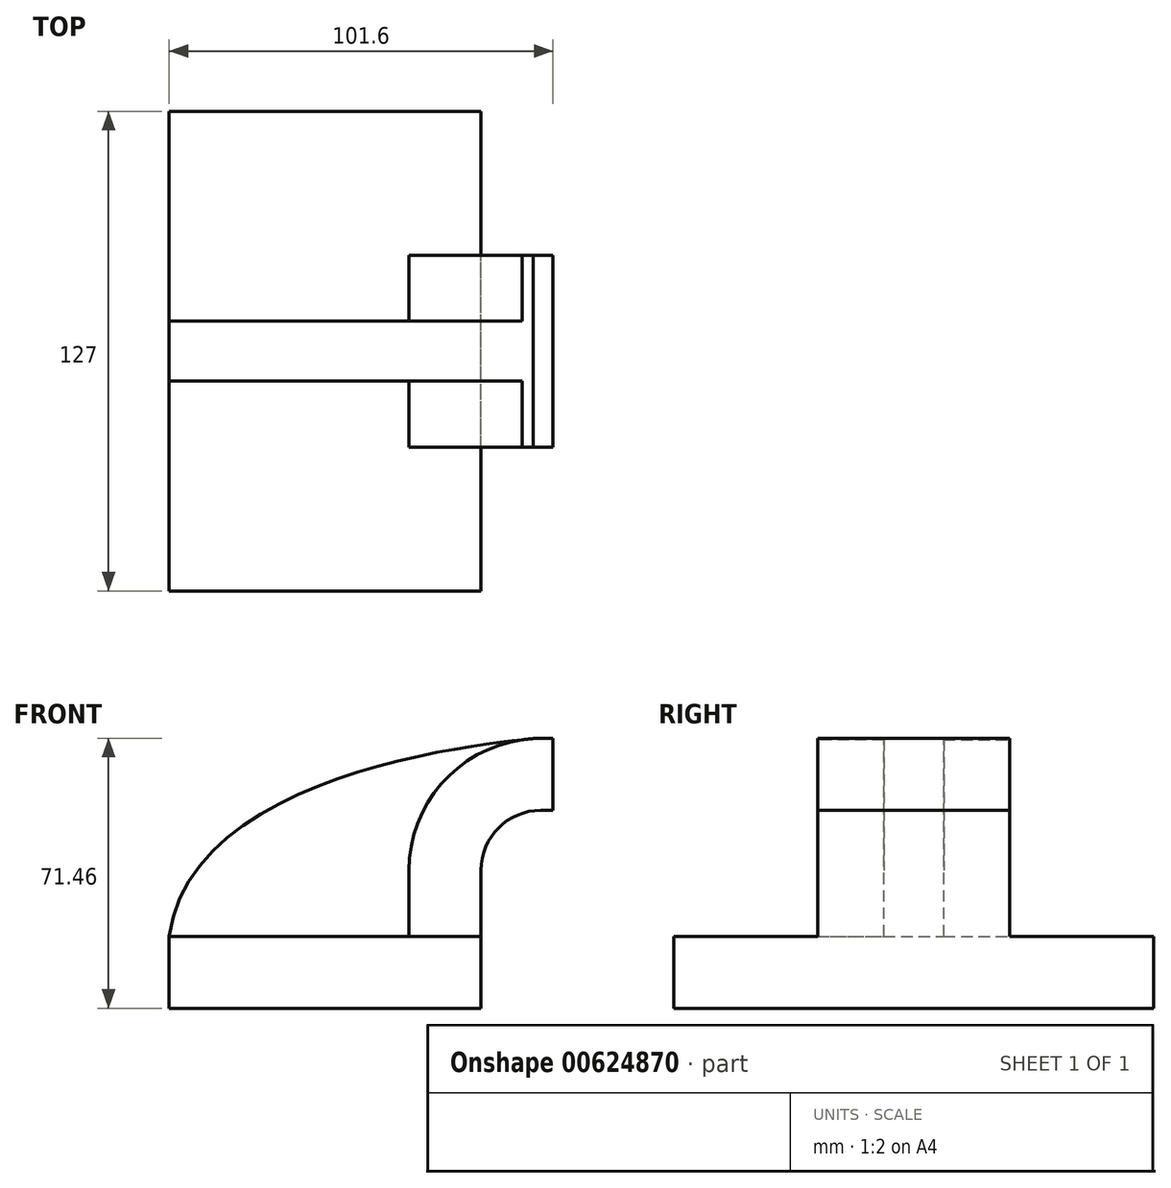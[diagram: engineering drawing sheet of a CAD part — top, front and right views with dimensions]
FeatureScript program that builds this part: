
annotation { "Feature Type Name" : "Feature", "Feature Type Description" : "" }
export const myFeature = defineFeature(function(context is Context, id is Id, definition is map)
    precondition{}
    {
        {
            var Q0;
            Q0=qCreatedBy(makeId("Front.planeOp"),FACE);
            var sketch = newSketch(context, id + "F0", { "sketchPlane" : qUnion([Q0])});
            skLineSegment(sketch, "E0.bottom", {"start": v(-41.28, -9.53) * mm, "end": v(41.28, -9.53) * mm});
            skLineSegment(sketch, "E0.top", {"start": v(-41.28, 9.52) * mm, "end": v(41.28, 9.52) * mm});
            skLineSegment(sketch, "E0.left", {"start": v(-41.28, -9.53) * mm, "end": v(-41.28, 9.53) * mm});
            skLineSegment(sketch, "E0.right", {"start": v(41.28, -9.53) * mm, "end": v(41.28, 9.52) * mm});
            skPoint(sketch, "E0.middle", {"position": v(0, 0) * mm});
            skLineSegment(sketch, "E1.bottom", {"start": v(60.32, 38.1) * mm, "end": v(111.12, 38.1) * mm});
            skLineSegment(sketch, "E1.top", {"start": v(60.32, 66.67) * mm, "end": v(111.12, 66.67) * mm});
            skLineSegment(sketch, "E1.left", {"start": v(60.32, 38.1) * mm, "end": v(60.32, 66.67) * mm});
            skLineSegment(sketch, "E1.right", {"start": v(111.12, 38.1) * mm, "end": v(111.12, 66.67) * mm});
            skPoint(sketch, "E1.middle", {"position": v(85.72, 52.39) * mm});
            skLineSegment(sketch, "E2", {"start": v(41.27, 9.52) * mm, "end": v(41.27, 27) * mm});
            skArc(sketch, "E3", {"start": v(41.27, 27) * mm, "mid": v(45.92, 38.23) * mm, "end": v(57.15, 42.88) * mm});
            skLineSegment(sketch, "E4", {"start": v(57.15, 42.88) * mm, "end": v(77.32, 42.88) * mm});
            skLineSegment(sketch, "E5.0", {"start": v(57.15, 61.93) * mm, "end": v(77.32, 61.93) * mm});
            skArc(sketch, "E5.1", {"start": v(22.22, 27) * mm, "mid": v(32.45, 51.7) * mm, "end": v(57.15, 61.93) * mm});
            skLineSegment(sketch, "E5.2", {"start": v(22.22, 9.52) * mm, "end": v(22.22, 27) * mm});
            skLineSegment(sketch, "E6", {"start": v(77.45, 66.67) * mm, "end": v(77.32, 38.1) * mm});
            skFitSpline(sketch, "E7", {"points": [v(-41.28, 9.53) * mm, v(55.13, 61.87) * mm, v(57.15, 61.93) * mm], "startDerivative": vector(19.51, 150.13) * mm, "endDerivative": vector(10.71, -2.97) * mm});
            skSolve(sketch);
        }
        {
            var Q0;
            Q0=makeQuery(id+"F0.imprint","IMPRINT",FACE,{"disambiguationData":[TD([[makeQuery(id+"F0.imprint","IMPRINT",EDGE,{"derivedFrom":sQuery(id+"F0.wireOp",EDGE,"E0.bottom")}),1.0]])]});
            extrude(context, id + "F1", {"entities" : qUnion([Q0]), "endBound" : BoundingType.SYMMETRIC, "depth" : 127 * mm, "offsetDistance" : 25.4 * mm});
        }
        {
            var Q0;
            {var subQ1=sQuery(id+"F0.wireOp",EDGE,"E2");Q0=makeQuery(id+"F0.imprint","IMPRINT",FACE,{"disambiguationData":[TD([[makeQuery(id+"F0.imprint","IMPRINT",EDGE,{"derivedFrom":subQ1}),1.0]])]});}
            extrude(context, id + "F2", {"entities" : qUnion([Q0]), "operationType" : NewBodyOperationType.ADD, "endBound" : BoundingType.SYMMETRIC, "depth" : 50.8 * mm, "offsetDistance" : 25.4 * mm});
        }
        {
            var Q0;
            {var subQ3=sQuery(id+"F0.wireOp",EDGE,"E5.2");Q0=makeQuery(id+"F0.imprint","IMPRINT",FACE,{"disambiguationData":[TD([[makeQuery(id+"F0.imprint","IMPRINT",EDGE,{"derivedFrom":subQ3}),1.0]])]});}
            extrude(context, id + "F3", {"entities" : qUnion([Q0]), "operationType" : NewBodyOperationType.ADD, "endBound" : BoundingType.SYMMETRIC, "depth" : 15.88 * mm, "offsetDistance" : 25.4 * mm});
        }
    });
